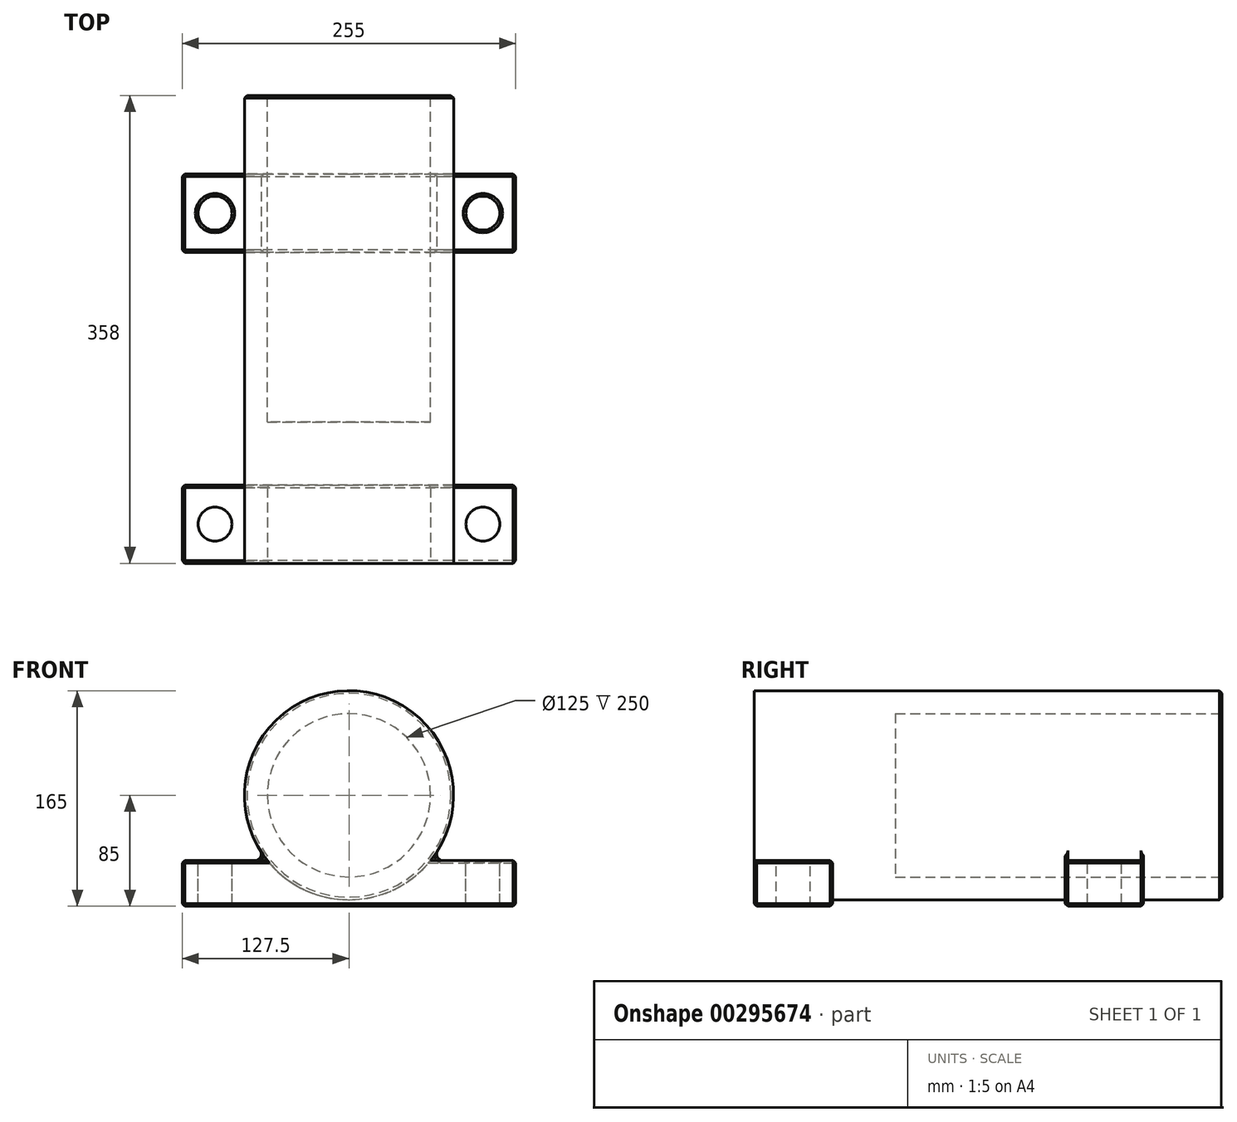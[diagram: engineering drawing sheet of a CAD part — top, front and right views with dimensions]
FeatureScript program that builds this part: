
annotation { "Feature Type Name" : "Feature", "Feature Type Description" : "" }
export const myFeature = defineFeature(function(context is Context, id is Id, definition is map)
    precondition{}
    {
        {
            var Q0;
            Q0=qCreatedBy(makeId("Front.planeOp"),FACE);
            var sketch = newSketch(context, id + "F0", { "sketchPlane" : qUnion([Q0])});
            skLineSegment(sketch, "E0", {"start": v(0, 75.3) * mm, "end": v(0, -85) * mm, "construction": true});
            skLineSegment(sketch, "E1", {"start": v(75.65, 0) * mm, "end": v(-74.59, 0) * mm, "construction": true});
            skLineSegment(sketch, "E2", {"start": v(0, -85) * mm, "end": v(-127.5, -85) * mm});
            skLineSegment(sketch, "E3", {"start": v(-127.5, -85) * mm, "end": v(-127.5, -50) * mm});
            skLineSegment(sketch, "E4", {"start": v(-127.5, -50) * mm, "end": v(127.5, -50) * mm});
            skLineSegment(sketch, "E5", {"start": v(127.5, -50) * mm, "end": v(127.5, -85) * mm});
            skLineSegment(sketch, "E6", {"start": v(127.5, -85) * mm, "end": v(0, -85) * mm});
            skLineSegment(sketch, "E7", {"start": v(-102.5, -65.8) * mm, "end": v(-102.5, -50) * mm, "construction": true});
            skLineSegment(sketch, "E8", {"start": v(-102.5, -35.04) * mm, "end": v(-102.5, -97.5) * mm, "construction": true});
            skLineSegment(sketch, "E9.MirrorCS", {"start": v(102.5, -35.04) * mm, "end": v(102.5, -97.5) * mm, "construction": true});
            skCircle(sketch, "E10", {"center": v(0, 0) * mm, "radius": 80 * mm});
            skPoint(sketch, "E11", {"position": v(102.5, -50) * mm});
            skPoint(sketch, "E12", {"position": v(-102.5, -50) * mm});
            skSolve(sketch);
        }
        {
            var Q0;
            Q0=qCreatedBy(makeId("Right.planeOp"),FACE);
            var sketch = newSketch(context, id + "F1", { "sketchPlane" : qUnion([Q0])});
            skLineSegment(sketch, "E13", {"start": v(0, 0) * mm, "end": v(442.27, 0) * mm, "construction": true});
            skSolve(sketch);
        }
        {
            var Q0;
            {var subQ0=sQuery(id+"F0.wireOp",EDGE,"E10");var subQ1=sQuery(id+"F0.wireOp",EDGE,"E4");var subQ2=makeQuery(id+"F0.imprint","INTERSECT",VERTEX,{"disambiguationData":[OD(0.0)],"derivedFrom":[subQ1,subQ0]});Q0=makeQuery(id+"F0.imprint","IMPRINT",FACE,{"disambiguationData":[TD([[makeQuery(id+"F0.imprint","IMPRINT",EDGE,{"disambiguationData":[TD([[subQ2,-1.0]])],"derivedFrom":subQ1}),1.0]])]});}
            var Q1;
            {var subQ0=sQuery(id+"F0.wireOp",EDGE,"E10");var subQ1=sQuery(id+"F0.wireOp",EDGE,"E4");var subQ2=makeQuery(id+"F0.imprint","INTERSECT",VERTEX,{"disambiguationData":[OD(0.0)],"derivedFrom":[subQ1,subQ0]});Q1=makeQuery(id+"F0.imprint","IMPRINT",FACE,{"disambiguationData":[TD([[makeQuery(id+"F0.imprint","IMPRINT",EDGE,{"disambiguationData":[TD([[subQ2,-1.0]])],"derivedFrom":subQ1}),-1.0]])]});}
            extrude(context, id + "F2", {"entities" : qUnion([Q0, Q1]), "oppositeDirection" : true, "depth" : 358 * mm});
        }
        {
            var Q0;
            Q0=makeQuery(id+"F0.imprint","IMPRINT",FACE,{"disambiguationData":[TD([[makeQuery(id+"F0.imprint","IMPRINT",EDGE,{"derivedFrom":sQuery(id+"F0.wireOp",EDGE,"E2")}),-1.0]])]});
            extrude(context, id + "F3", {"entities" : qUnion([Q0]), "operationType" : NewBodyOperationType.ADD, "oppositeDirection" : true, "depth" : 60 * mm});
        }
        {
            var Q0;
            {var subQ0=sQuery(id+"F0.wireOp",EDGE,"E4");Q0=makeQuery(id+"F3.opExtrude","SWEPT_FACE",FACE,{"disambiguationData":[OSD([subQ0]),TDD([makeQuery(id+"F0.imprint","IMPRINT",EDGE,{"disambiguationData":[TD([[makeQuery(id+"F0.imprint","INTERSECT",VERTEX,{"derivedFrom":[subQ0,sQuery(id+"F0.wireOp",EDGE,"E5")]}),1.0]])],"derivedFrom":subQ0})])]});}
            var sketch = newSketch(context, id + "F4", { "sketchPlane" : qUnion([Q0])});
            skLineSegment(sketch, "E14", {"start": v(127.5, 30) * mm, "end": v(102.5, 30) * mm, "construction": true});
            skPoint(sketch, "E15", {"position": v(102.5, 30) * mm});
            skLineSegment(sketch, "E16", {"start": v(102.5, 30) * mm, "end": v(102.5, 268) * mm, "construction": true});
            skPoint(sketch, "E17", {"position": v(102.5, 268) * mm});
            skLineSegment(sketch, "E18", {"start": v(102.5, 268) * mm, "end": v(127.5, 268) * mm, "construction": true});
            skLineSegment(sketch, "E19", {"start": v(127.5, 268) * mm, "end": v(127.5, 238) * mm});
            skLineSegment(sketch, "E20", {"start": v(127.5, 238) * mm, "end": v(-127.5, 238) * mm});
            skLineSegment(sketch, "E21", {"start": v(-127.5, 238) * mm, "end": v(-127.5, 298) * mm});
            skLineSegment(sketch, "E22", {"start": v(-127.5, 298) * mm, "end": v(127.5, 298) * mm});
            skLineSegment(sketch, "E23", {"start": v(127.5, 298) * mm, "end": v(127.5, 268) * mm});
            skPoint(sketch, "E24.MirrorP", {"position": v(-102.5, 268) * mm});
            skPoint(sketch, "E25.MirrorP", {"position": v(-102.5, 30) * mm});
            skCircle(sketch, "E26", {"center": v(-102.5, 268) * mm, "radius": 13 * mm});
            skCircle(sketch, "E27", {"center": v(102.5, 268) * mm, "radius": 13 * mm});
            skCircle(sketch, "E28", {"center": v(-102.5, 30) * mm, "radius": 13 * mm});
            skCircle(sketch, "E29", {"center": v(102.5, 30) * mm, "radius": 13 * mm});
            skSolve(sketch);
        }
        {
            var Q0;
            Q0=makeQuery(id+"F4.imprint","IMPRINT",FACE,{"disambiguationData":[TD([[makeQuery(id+"F4.imprint","IMPRINT",EDGE,{"derivedFrom":sQuery(id+"F4.wireOp",EDGE,"E19")}),-1.0]])]});
            extrude(context, id + "F5", {"entities" : qUnion([Q0]), "operationType" : NewBodyOperationType.ADD, "oppositeDirection" : true, "depth" : 35 * mm});
        }
        {
            var Q0;
            Q0=makeQuery(id+"F4.imprint","IMPRINT",FACE,{"disambiguationData":[TD([[makeQuery(id+"F4.imprint","IMPRINT",EDGE,{"derivedFrom":sQuery(id+"F4.wireOp",EDGE,"E28")}),1.0]])]});
            var Q1;
            Q1=makeQuery(id+"F4.imprint","IMPRINT",FACE,{"disambiguationData":[TD([[makeQuery(id+"F4.imprint","IMPRINT",EDGE,{"derivedFrom":sQuery(id+"F4.wireOp",EDGE,"E29")}),1.0]])]});
            extrude(context, id + "F6", {"entities" : qUnion([Q0, Q1]), "operationType" : NewBodyOperationType.REMOVE, "oppositeDirection" : true, "depth" : 35 * mm});
        }
        {
            var Q0;
            Q0=makeQuery(id+"F2.opExtrude","CAP_FACE",FACE,{"disambiguationData":[OSD([sQuery(id+"F0.wireOp",EDGE,"E10")])],"isStart":false});
            var sketch = newSketch(context, id + "F7", { "sketchPlane" : qUnion([Q0])});
            skCircle(sketch, "E30", {"center": v(0, 0) * mm, "radius": 62.5 * mm});
            skSolve(sketch);
        }
        {
            var Q0;
            Q0=makeQuery(id+"F7.imprint","IMPRINT",FACE,{"disambiguationData":[TD([[makeQuery(id+"F7.imprint","IMPRINT",EDGE,{"derivedFrom":sQuery(id+"F7.wireOp",EDGE,"E30")}),1.0]])]});
            extrude(context, id + "F8", {"entities" : qUnion([Q0]), "operationType" : NewBodyOperationType.REMOVE, "oppositeDirection" : true, "depth" : 250 * mm});
        }
        {
            var Q0;
            {var subQ0=sQuery(id+"F0.wireOp",EDGE,"E10");var subQ1=sQuery(id+"F0.wireOp",EDGE,"E4");Q0=makeQuery(id+"F3.opExtrude","SWEPT_EDGE",EDGE,{"disambiguationData":[OSD([subQ1,subQ0]),TDD([makeQuery(id+"F0.imprint","INTERSECT",VERTEX,{"disambiguationData":[OD(1.0)],"derivedFrom":[subQ1,subQ0]})])]});}
            var Q1;
            Q1=makeQuery(id+"F5.boolean.opBoolean","INTERSECT",EDGE,{"disambiguationData":[OD(0.0)],"derivedFrom":[makeQuery(id+"F2.opExtrude","SWEPT_FACE",FACE,{"disambiguationData":[OSD([sQuery(id+"F0.wireOp",EDGE,"E10")])]}),makeQuery(id+"F5.opExtrude","CAP_FACE",FACE,{"disambiguationData":[OSD([sQuery(id+"F4.wireOp",EDGE,"E19"),sQuery(id+"F4.wireOp",EDGE,"E20"),sQuery(id+"F4.wireOp",EDGE,"E21"),sQuery(id+"F4.wireOp",EDGE,"E22"),sQuery(id+"F4.wireOp",EDGE,"E23"),sQuery(id+"F4.wireOp",EDGE,"E26"),sQuery(id+"F4.wireOp",EDGE,"E27")])],"isStart":true})]});
            var Q2;
            {var subQ0=sQuery(id+"F0.wireOp",EDGE,"E10");var subQ1=sQuery(id+"F0.wireOp",EDGE,"E4");Q2=makeQuery(id+"F3.opExtrude","SWEPT_EDGE",EDGE,{"disambiguationData":[OSD([subQ1,subQ0]),TDD([makeQuery(id+"F0.imprint","INTERSECT",VERTEX,{"disambiguationData":[OD(0.0)],"derivedFrom":[subQ1,subQ0]})])]});}
            var Q3;
            Q3=makeQuery(id+"F5.boolean.opBoolean","INTERSECT",EDGE,{"disambiguationData":[OD(1.0)],"derivedFrom":[makeQuery(id+"F2.opExtrude","SWEPT_FACE",FACE,{"disambiguationData":[OSD([sQuery(id+"F0.wireOp",EDGE,"E10")])]}),makeQuery(id+"F5.opExtrude","CAP_FACE",FACE,{"disambiguationData":[OSD([sQuery(id+"F4.wireOp",EDGE,"E19"),sQuery(id+"F4.wireOp",EDGE,"E20"),sQuery(id+"F4.wireOp",EDGE,"E21"),sQuery(id+"F4.wireOp",EDGE,"E22"),sQuery(id+"F4.wireOp",EDGE,"E23"),sQuery(id+"F4.wireOp",EDGE,"E26"),sQuery(id+"F4.wireOp",EDGE,"E27")])],"isStart":true})]});
            fillet(context, id + "F9", {"entities" : qUnion([Q0, Q1, Q2, Q3]), "radius" : 5 * mm, "tangentPropagation" : true, "allowEdgeOverflow" : false});
        }
        {
            var Q0;
            {var subQ0=sQuery(id+"F4.wireOp",EDGE,"E21");var subQ1=sQuery(id+"F4.wireOp",EDGE,"E20");Q0=makeQuery(id+"F5.boolean.opBoolean","SPLIT",EDGE,{"disambiguationData":[TD([makeQuery(id+"F5.opExtrude","SWEPT_FACE",FACE,{"disambiguationData":[OSD([subQ0])]})])],"derivedFrom":makeQuery(id+"F5.opExtrude","CAP_EDGE",EDGE,{"disambiguationData":[OSD([subQ1])],"isStart":true})});}
            var Q1;
            Q1=makeQuery(id+"F5.opExtrude","CAP_EDGE",EDGE,{"disambiguationData":[OSD([sQuery(id+"F4.wireOp",EDGE,"E21")])],"isStart":true});
            var Q2;
            {var subQ0=sQuery(id+"F4.wireOp",EDGE,"E22");var subQ1=sQuery(id+"F4.wireOp",EDGE,"E21");Q2=makeQuery(id+"F5.boolean.opBoolean","SPLIT",EDGE,{"disambiguationData":[TD([makeQuery(id+"F5.opExtrude","SWEPT_FACE",FACE,{"disambiguationData":[OSD([subQ1])]})])],"derivedFrom":makeQuery(id+"F5.opExtrude","CAP_EDGE",EDGE,{"disambiguationData":[OSD([subQ0])],"isStart":true})});}
            var Q3;
            Q3=makeQuery(id+"F5.opExtrude","SWEPT_EDGE",EDGE,{"disambiguationData":[OSD([sQuery(id+"F4.wireOp",EDGE,"E20"),sQuery(id+"F4.wireOp",EDGE,"E21")])]});
            var Q4;
            Q4=makeQuery(id+"F5.opExtrude","SWEPT_EDGE",EDGE,{"disambiguationData":[OSD([sQuery(id+"F4.wireOp",EDGE,"E21"),sQuery(id+"F4.wireOp",EDGE,"E22")])]});
            var Q5;
            Q5=makeQuery(id+"F5.opExtrude","CAP_EDGE",EDGE,{"disambiguationData":[OSD([sQuery(id+"F4.wireOp",EDGE,"E21")])],"isStart":false});
            var Q6;
            Q6=makeQuery(id+"F5.opExtrude","CAP_EDGE",EDGE,{"disambiguationData":[OSD([sQuery(id+"F4.wireOp",EDGE,"E20")])],"isStart":false});
            var Q7;
            Q7=makeQuery(id+"F5.opExtrude","CAP_EDGE",EDGE,{"disambiguationData":[OSD([sQuery(id+"F4.wireOp",EDGE,"E22")])],"isStart":false});
            var Q8;
            {var subQ0=sQuery(id+"F4.wireOp",EDGE,"E23");var subQ1=sQuery(id+"F4.wireOp",EDGE,"E22");var subQ2=sQuery(id+"F4.wireOp",EDGE,"E19");Q8=makeQuery(id+"F5.boolean.opBoolean","SPLIT",EDGE,{"disambiguationData":[TD([makeQuery(id+"F5.opExtrude","SWEPT_FACE",FACE,{"disambiguationData":[OSD([subQ2,subQ0])]})])],"derivedFrom":makeQuery(id+"F5.opExtrude","CAP_EDGE",EDGE,{"disambiguationData":[OSD([subQ1])],"isStart":true})});}
            var Q9;
            Q9=makeQuery(id+"F5.opExtrude","SWEPT_EDGE",EDGE,{"disambiguationData":[OSD([sQuery(id+"F4.wireOp",EDGE,"E22"),sQuery(id+"F4.wireOp",EDGE,"E23")])]});
            var Q10;
            Q10=makeQuery(id+"F5.opExtrude","CAP_EDGE",EDGE,{"disambiguationData":[OSD([sQuery(id+"F4.wireOp",EDGE,"E19"),sQuery(id+"F4.wireOp",EDGE,"E23")])],"isStart":false});
            var Q11;
            Q11=makeQuery(id+"F5.opExtrude","SWEPT_EDGE",EDGE,{"disambiguationData":[OSD([sQuery(id+"F4.wireOp",EDGE,"E19"),sQuery(id+"F4.wireOp",EDGE,"E20")])]});
            var Q12;
            Q12=makeQuery(id+"F5.opExtrude","CAP_EDGE",EDGE,{"disambiguationData":[OSD([sQuery(id+"F4.wireOp",EDGE,"E19"),sQuery(id+"F4.wireOp",EDGE,"E23")])],"isStart":true});
            var Q13;
            {var subQ0=sQuery(id+"F4.wireOp",EDGE,"E23");var subQ1=sQuery(id+"F4.wireOp",EDGE,"E20");var subQ2=sQuery(id+"F4.wireOp",EDGE,"E19");Q13=makeQuery(id+"F5.boolean.opBoolean","SPLIT",EDGE,{"disambiguationData":[TD([makeQuery(id+"F5.opExtrude","SWEPT_FACE",FACE,{"disambiguationData":[OSD([subQ2,subQ0])]})])],"derivedFrom":makeQuery(id+"F5.opExtrude","CAP_EDGE",EDGE,{"disambiguationData":[OSD([subQ1])],"isStart":true})});}
            var Q14;
            Q14=makeQuery(id+"F3.opExtrude","CAP_EDGE",EDGE,{"disambiguationData":[OSD([sQuery(id+"F0.wireOp",EDGE,"E3")])],"isStart":false});
            var Q15;
            Q15=makeQuery(id+"F3.opExtrude","SWEPT_EDGE",EDGE,{"disambiguationData":[OSD([sQuery(id+"F0.wireOp",EDGE,"E3"),sQuery(id+"F0.wireOp",EDGE,"E4")])]});
            var Q16;
            Q16=makeQuery(id+"F3.opExtrude","CAP_EDGE",EDGE,{"disambiguationData":[OSD([sQuery(id+"F0.wireOp",EDGE,"E3")])],"isStart":true});
            var Q17;
            Q17=makeQuery(id+"F3.opExtrude","SWEPT_EDGE",EDGE,{"disambiguationData":[OSD([sQuery(id+"F0.wireOp",EDGE,"E2"),sQuery(id+"F0.wireOp",EDGE,"E3")])]});
            var Q18;
            {var subQ0=sQuery(id+"F0.wireOp",EDGE,"E4");Q18=makeQuery(id+"F3.opExtrude","CAP_EDGE",EDGE,{"disambiguationData":[OSD([subQ0]),TDD([makeQuery(id+"F0.imprint","IMPRINT",EDGE,{"disambiguationData":[TD([[makeQuery(id+"F0.imprint","INTERSECT",VERTEX,{"derivedFrom":[sQuery(id+"F0.wireOp",EDGE,"E3"),subQ0]}),-1.0]])],"derivedFrom":subQ0})])],"isStart":true});}
            var Q19;
            {var subQ0=sQuery(id+"F0.wireOp",EDGE,"E4");Q19=makeQuery(id+"F3.opExtrude","CAP_EDGE",EDGE,{"disambiguationData":[OSD([subQ0]),TDD([makeQuery(id+"F0.imprint","IMPRINT",EDGE,{"disambiguationData":[TD([[makeQuery(id+"F0.imprint","INTERSECT",VERTEX,{"derivedFrom":[sQuery(id+"F0.wireOp",EDGE,"E3"),subQ0]}),-1.0]])],"derivedFrom":subQ0})])],"isStart":false});}
            var Q20;
            Q20=makeQuery(id+"F3.opExtrude","CAP_EDGE",EDGE,{"disambiguationData":[OSD([sQuery(id+"F0.wireOp",EDGE,"E2"),sQuery(id+"F0.wireOp",EDGE,"E6")])],"isStart":false});
            var Q21;
            Q21=makeQuery(id+"F6.boolean.opBoolean","COPY",EDGE,{"derivedFrom":makeQuery(id+"F6.opExtrude","CAP_EDGE",EDGE,{"disambiguationData":[OSD([sQuery(id+"F4.wireOp",EDGE,"E28")])],"isStart":true})});
            var Q22;
            Q22=makeQuery(id+"F5.opExtrude","CAP_EDGE",EDGE,{"disambiguationData":[OSD([sQuery(id+"F4.wireOp",EDGE,"E26")])],"isStart":true});
            var Q23;
            Q23=makeQuery(id+"F3.opExtrude","CAP_EDGE",EDGE,{"disambiguationData":[OSD([sQuery(id+"F0.wireOp",EDGE,"E2"),sQuery(id+"F0.wireOp",EDGE,"E6")])],"isStart":true});
            var Q24;
            Q24=makeQuery(id+"F3.opExtrude","SWEPT_EDGE",EDGE,{"disambiguationData":[OSD([sQuery(id+"F0.wireOp",EDGE,"E4"),sQuery(id+"F0.wireOp",EDGE,"E5")])]});
            var Q25;
            Q25=makeQuery(id+"F3.opExtrude","CAP_EDGE",EDGE,{"disambiguationData":[OSD([sQuery(id+"F0.wireOp",EDGE,"E5")])],"isStart":true});
            var Q26;
            Q26=makeQuery(id+"F3.opExtrude","SWEPT_EDGE",EDGE,{"disambiguationData":[OSD([sQuery(id+"F0.wireOp",EDGE,"E5"),sQuery(id+"F0.wireOp",EDGE,"E6")])]});
            var Q27;
            Q27=makeQuery(id+"F3.opExtrude","CAP_EDGE",EDGE,{"disambiguationData":[OSD([sQuery(id+"F0.wireOp",EDGE,"E5")])],"isStart":false});
            var Q28;
            {var subQ0=sQuery(id+"F0.wireOp",EDGE,"E4");Q28=makeQuery(id+"F3.opExtrude","CAP_EDGE",EDGE,{"disambiguationData":[OSD([subQ0]),TDD([makeQuery(id+"F0.imprint","IMPRINT",EDGE,{"disambiguationData":[TD([[makeQuery(id+"F0.imprint","INTERSECT",VERTEX,{"derivedFrom":[subQ0,sQuery(id+"F0.wireOp",EDGE,"E5")]}),1.0]])],"derivedFrom":subQ0})])],"isStart":false});}
            var Q29;
            Q29=makeQuery(id+"F6.boolean.opBoolean","COPY",EDGE,{"derivedFrom":makeQuery(id+"F6.opExtrude","CAP_EDGE",EDGE,{"disambiguationData":[OSD([sQuery(id+"F4.wireOp",EDGE,"E29")])],"isStart":true})});
            var Q30;
            Q30=makeQuery(id+"F5.opExtrude","CAP_EDGE",EDGE,{"disambiguationData":[OSD([sQuery(id+"F4.wireOp",EDGE,"E27")])],"isStart":true});
            var Q31;
            Q31=makeQuery(id+"F5.opExtrude","CAP_EDGE",EDGE,{"disambiguationData":[OSD([sQuery(id+"F4.wireOp",EDGE,"E27")])],"isStart":false});
            var Q32;
            Q32=makeQuery(id+"F5.opExtrude","CAP_EDGE",EDGE,{"disambiguationData":[OSD([sQuery(id+"F4.wireOp",EDGE,"E26")])],"isStart":false});
            var Q33;
            Q33=makeQuery(id+"F6.boolean.opBoolean","COPY",EDGE,{"derivedFrom":makeQuery(id+"F6.opExtrude","CAP_EDGE",EDGE,{"disambiguationData":[OSD([sQuery(id+"F4.wireOp",EDGE,"E29")])],"isStart":false})});
            var Q34;
            Q34=makeQuery(id+"F6.boolean.opBoolean","COPY",EDGE,{"derivedFrom":makeQuery(id+"F6.opExtrude","CAP_EDGE",EDGE,{"disambiguationData":[OSD([sQuery(id+"F4.wireOp",EDGE,"E28")])],"isStart":false})});
            var Q35;
            Q35=makeQuery(id+"F2.opExtrude","CAP_EDGE",EDGE,{"disambiguationData":[OSD([sQuery(id+"F0.wireOp",EDGE,"E10")])],"isStart":false});
            var Q36;
            Q36=makeQuery(id+"F8.boolean.opBoolean","COPY",EDGE,{"derivedFrom":makeQuery(id+"F8.opExtrude","CAP_EDGE",EDGE,{"disambiguationData":[OSD([sQuery(id+"F7.wireOp",EDGE,"E30")])],"isStart":true})});
            chamfer(context, id + "F10", {"entities" : qUnion([Q0, Q1, Q2, Q3, Q4, Q5, Q6, Q7, Q8, Q9, Q10, Q11, Q12, Q13, Q14, Q15, Q16, Q17, Q18, Q19, Q20, Q21, Q22, Q23, Q24, Q25, Q26, Q27, Q28, Q29, Q30, Q31, Q32, Q33, Q34, Q35, Q36]), "width" : 2 * mm, "tangentPropagation" : true});
        }
    });
